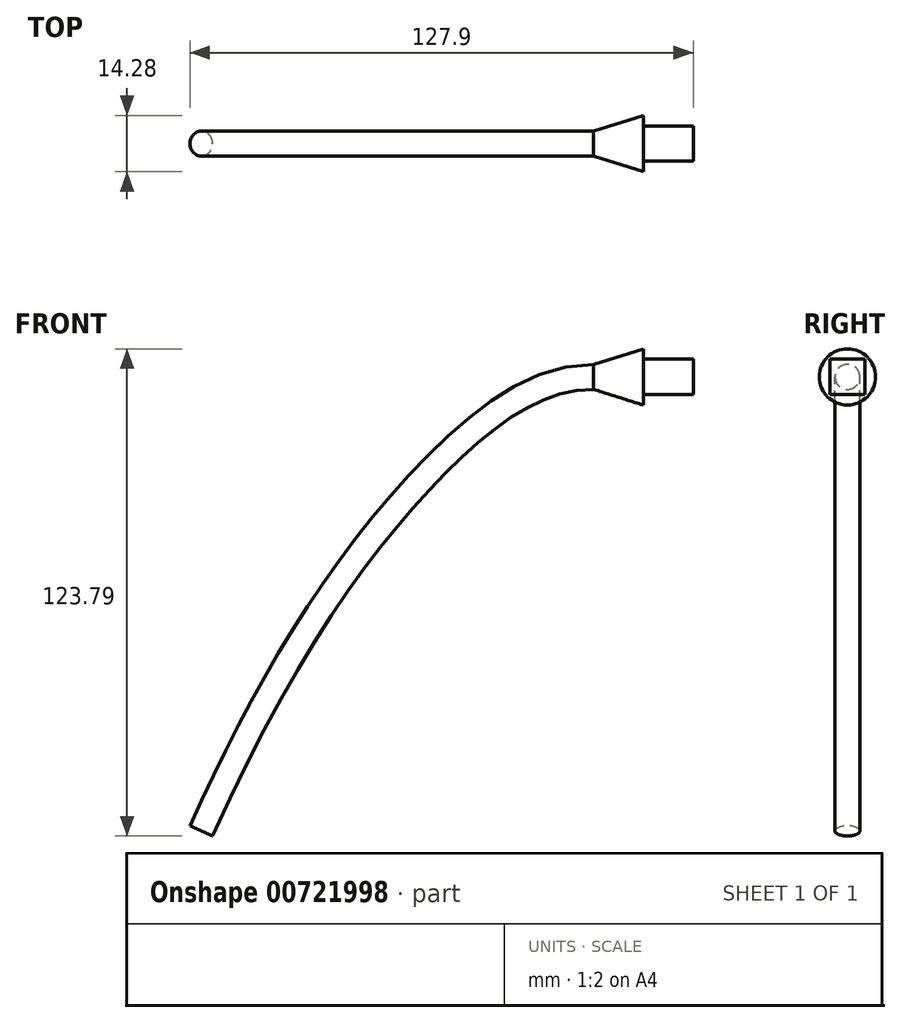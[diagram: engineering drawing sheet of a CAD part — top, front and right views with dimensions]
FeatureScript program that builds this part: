
annotation { "Feature Type Name" : "Feature", "Feature Type Description" : "" }
export const myFeature = defineFeature(function(context is Context, id is Id, definition is map)
    precondition{}
    {
        {
            var Q0;
            Q0=qCreatedBy(makeId("Right.planeOp"),FACE);
            var sketch = newSketch(context, id + "F0", { "sketchPlane" : qUnion([Q0])});
            skCircle(sketch, "E0", {"center": v(0, 0) * mm, "radius": 3.18 * mm});
            skSolve(sketch);
        }
        {
            var Q0;
            Q0=qCreatedBy(makeId("Front.planeOp"),FACE);
            var sketch = newSketch(context, id + "F1", { "sketchPlane" : qUnion([Q0])});
            skFitSpline(sketch, "E1", {"points": [v(0, 0) * mm, v(-39.66, -22.08) * mm, v(-99.6, -115.35) * mm], "startDerivative": vector(-111.3, 0) * mm, "endDerivative": vector(-102.04, -226.13) * mm});
            skSolve(sketch);
        }
        {
            var Q0;
            Q0 = qSketchRegion(id + "F0", true);
            var Q1;
            Q1 = qConstructionFilter(qBodyType(qCreatedBy(id + "F1" ,EDGE), BodyType.WIRE), ConstructionObject.NO);
            sweep(context, id + "F2", {"profiles" : qUnion([Q0]), "path" : qUnion([Q1])});
        }
        {
            var Q0;
            Q0=qCreatedBy(makeId("Right.planeOp"),FACE);
            cPlane(context, id + "F3", {"entities" : qUnion([Q0]), "cplaneType" : CPlaneType.OFFSET, "offset" : 12.7 * mm, "width" : 152.4 * mm, "height" : 152.4 * mm});
        }
        {
            var Q0;
            Q0=qCreatedBy(id+"F3.planeOp",FACE);
            var sketch = newSketch(context, id + "F4", { "sketchPlane" : qUnion([Q0])});
            skCircle(sketch, "E2", {"center": v(0, 0) * mm, "radius": 7.14 * mm});
            skSolve(sketch);
        }
        {
            var Q0;
            Q0=qCreatedBy(id+"F3.planeOp",FACE);
            var sketch = newSketch(context, id + "F5", { "sketchPlane" : qUnion([Q0])});
            skLineSegment(sketch, "E3.bottom", {"start": v(4.5, -4.5) * mm, "end": v(-4.5, -4.5) * mm});
            skLineSegment(sketch, "E3.top", {"start": v(4.5, 4.5) * mm, "end": v(-4.5, 4.5) * mm});
            skLineSegment(sketch, "E3.left", {"start": v(4.5, -4.5) * mm, "end": v(4.5, 4.5) * mm});
            skLineSegment(sketch, "E3.right", {"start": v(-4.5, -4.5) * mm, "end": v(-4.5, 4.5) * mm});
            skPoint(sketch, "E3.middle", {"position": v(0, 0) * mm});
            skSolve(sketch);
        }
        {
            var Q1;
            Q1 = qSketchRegion(id + "F4", true);
            var Q2;
            Q2=makeQuery(id+"F2.opSweep","CAP_FACE",FACE,{"disambiguationData":[OSD([sQuery(id+"F0.wireOp",EDGE,"E0"),sQuery(id+"F1.wireOp",VERTEX,"E1.start")])],"isStart":true});
            loft(context, id + "F6", {"operationType" : NewBodyOperationType.ADD, "sheetProfilesArray" : [{ "sheetProfileEntities" : qUnion([Q1]) }, { "sheetProfileEntities" : qUnion([Q2]) }]});
        }
        {
            var Q0;
            Q0=makeQuery(id+"F5.imprint","IMPRINT",FACE,{"disambiguationData":[TD([[makeQuery(id+"F5.imprint","IMPRINT",EDGE,{"derivedFrom":sQuery(id+"F5.wireOp",EDGE,"E3.bottom")}),-1.0]])]});
            extrude(context, id + "F7", {"entities" : qUnion([Q0]), "operationType" : NewBodyOperationType.ADD, "depth" : 12.7 * mm, "offsetDistance" : 25.4 * mm});
        }
    });
